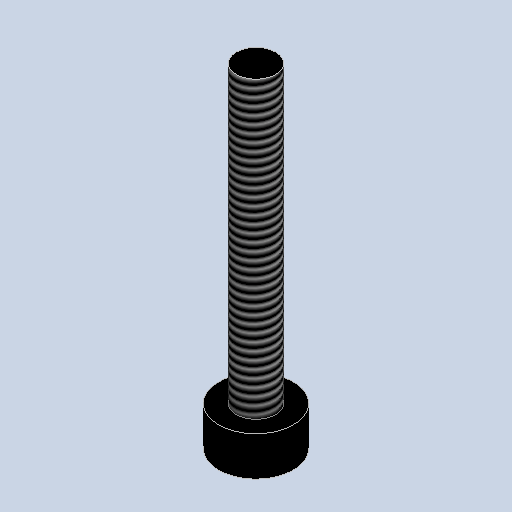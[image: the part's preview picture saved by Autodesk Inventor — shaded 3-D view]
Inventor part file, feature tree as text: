
AUTODESK INVENTOR PART (.ipt)
format: ipt  version: 2024.2 (Build 282272000, 272)  size: 300,544 bytes
history: native  units: mm
features: sketch x2, revolve x1, thread x1, extrude x1
ambient origin geometry x8: Origin, YZ Plane, XZ Plane, XY Plane, X Axis, Y Axis, Z Axis, Center Point
bodies: Solid1 (feature_tree)
feature tree (5):
  revolve  "Revolution1"  [1 undecoded]
  thread  "Thread1"  [1 undecoded]
  extrude  "Extrusion1"  [1 undecoded]
  sketch  "Sketch1"  dims[d4=90.0deg d5=10.0mm d6=0.0mm d0=0.0mm]
  sketch  "Sketch2"
note: 3 required parameter values undecoded (feature->parameter linkage not recoverable at this tier; creation-order binding heuristic only, values carry confidence <= 0.55)